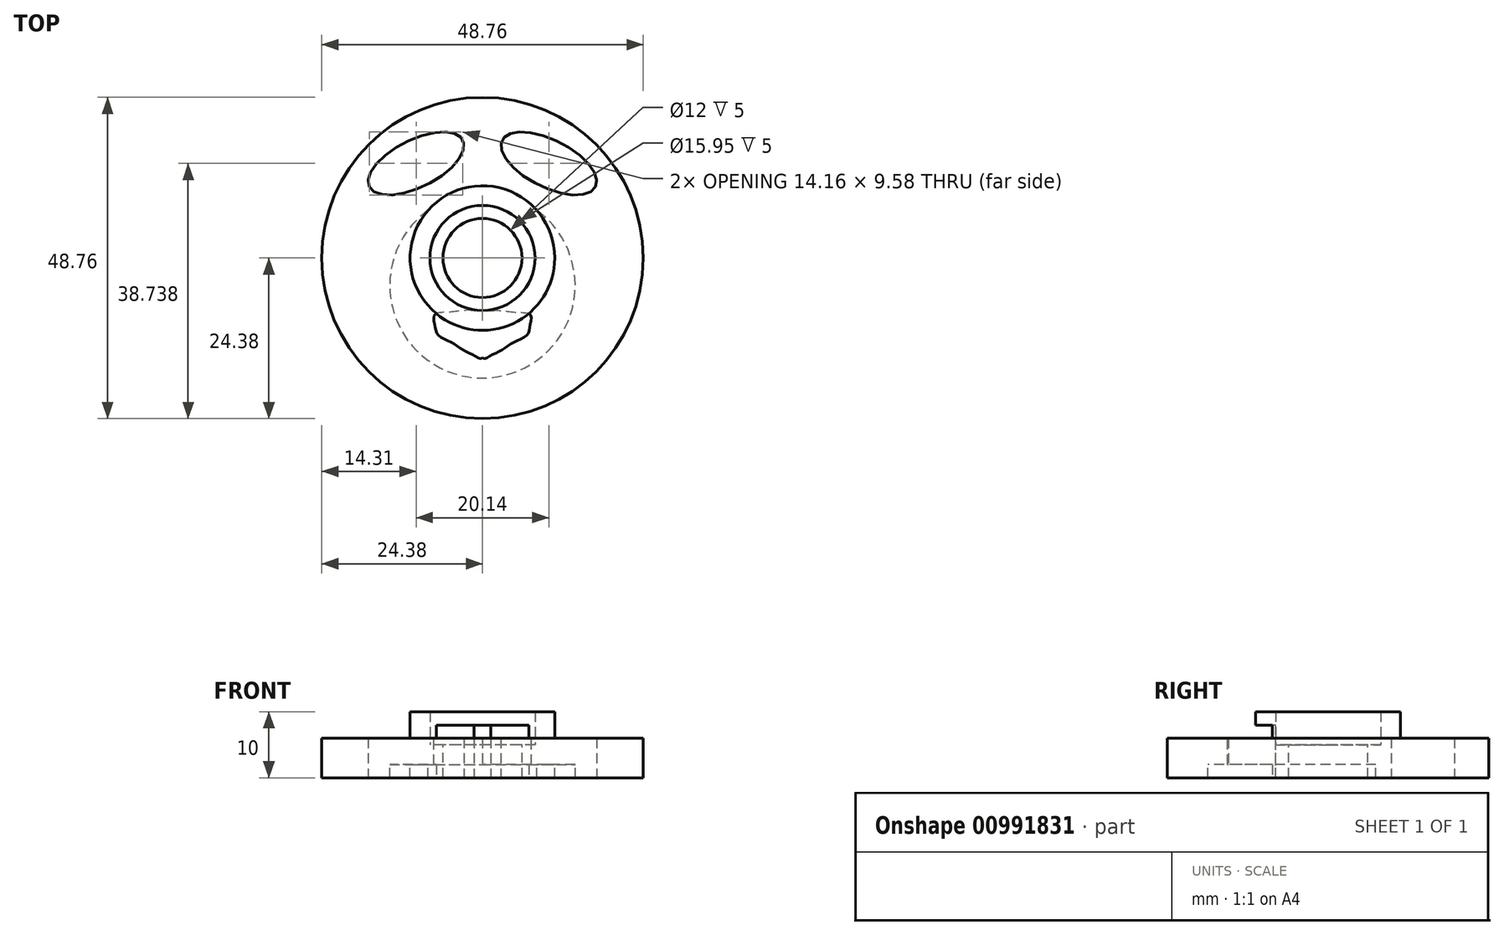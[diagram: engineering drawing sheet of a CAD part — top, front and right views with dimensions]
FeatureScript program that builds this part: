
annotation { "Feature Type Name" : "Feature", "Feature Type Description" : "" }
export const myFeature = defineFeature(function(context is Context, id is Id, definition is map)
    precondition{}
    {
        {
            var Q0;
            Q0=qCreatedBy(makeId("Top.planeOp"),FACE);
            var sketch = newSketch(context, id + "F0", { "sketchPlane" : qUnion([Q0])});
            skCircle(sketch, "E0", {"center": v(0, 0) * mm, "radius": 24.38 * mm});
            skSolve(sketch);
        }
        {
            var Q0;
            Q0=makeQuery(id+"F0.imprint","IMPRINT",FACE,{"disambiguationData":[TD([[makeQuery(id+"F0.imprint","IMPRINT",EDGE,{"derivedFrom":sQuery(id+"F0.wireOp",EDGE,"E0")}),1.0]])]});
            extrude(context, id + "F1", {"entities" : qUnion([Q0]), "depth" : 4 * mm, "offsetDistance" : 25.4 * mm});
        }
        {
            var Q0;
            Q0=makeQuery(id+"F1.opExtrude","CAP_FACE",FACE,{"disambiguationData":[OSD([sQuery(id+"F0.wireOp",EDGE,"E0"),sQuery(id+"F0.wireOp",EDGE,"n39IqKt5-bk1q-LU1x-fgod-8OyBNiFTd7FZ")])],"isStart":false});
            var sketch = newSketch(context, id + "F2", { "sketchPlane" : qUnion([Q0])});
            skCircle(sketch, "E1", {"center": v(0, 0) * mm, "radius": 7.97 * mm});
            skCircle(sketch, "E2.0", {"center": v(0, 0) * mm, "radius": 10.97 * mm});
            skSolve(sketch);
        }
        {
            var Q0;
            Q0=qSketchRegion(id+"F2",true);
            extrude(context, id + "F3", {"entities" : qUnion([Q0]), "operationType" : NewBodyOperationType.ADD, "depth" : 4 * mm, "offsetDistance" : 25.4 * mm});
        }
        {
            var Q0;
            Q0=makeQuery(id+"F3.boolean.opBoolean","SPLIT",FACE,{"disambiguationData":[TD([makeQuery(id+"F3.opExtrude","SWEPT_FACE",FACE,{"disambiguationData":[OSD([sQuery(id+"F2.wireOp",EDGE,"E1")])]})])],"derivedFrom":makeQuery(id+"F1.opExtrude","CAP_FACE",FACE,{"disambiguationData":[OSD([sQuery(id+"F0.wireOp",EDGE,"E0")])],"isStart":false})});
            var sketch = newSketch(context, id + "F4", { "sketchPlane" : qUnion([Q0])});
            skCircle(sketch, "E3", {"center": v(0, 0) * mm, "radius": 6 * mm});
            skSolve(sketch);
        }
        {
            var Q0;
            Q0=makeQuery(id+"F4.imprint","IMPRINT",FACE,{"disambiguationData":[TD([[makeQuery(id+"F4.imprint","IMPRINT",EDGE,{"derivedFrom":sQuery(id+"F4.wireOp",EDGE,"E3")}),1.0]])]});
            var Q1;
            Q1=makeQuery(id+"F4.imprint","IMPRINT",FACE,{"disambiguationData":[TD([[makeQuery(id+"F4.imprint","IMPRINT",EDGE,{"derivedFrom":makeQuery(id+"FgYK8jIepfClWtA_1.opExtrude","CAP_EDGE",EDGE,{"disambiguationData":[OSD([sQuery(id+"F8DXjnVyigKkjng_1.wireOp",EDGE,"EUjAMsCd-Zx2B-3j4q-cP5o-T3GrjTijNDqK")])],"isStart":false})}),1.0]])]});
            extrude(context, id + "F5", {"entities" : qUnion([Q0, Q1]), "operationType" : NewBodyOperationType.REMOVE, "oppositeDirection" : true, "depth" : 9 * mm, "offsetDistance" : 25.4 * mm});
        }
        {
            var Q0;
            Q0=qCreatedBy(makeId("Front.planeOp"),FACE);
            var sketch = newSketch(context, id + "F6", { "sketchPlane" : qUnion([Q0])});
            skCircle(sketch, "E4", {"center": v(-24.38, 2) * mm, "radius": 1.5 * mm});
            skLineSegment(sketch, "E5.bottom", {"start": v(-22.88, 0.65) * mm, "end": v(-25.02, 0.65) * mm});
            skLineSegment(sketch, "E5.top", {"start": v(-22.88, 3.35) * mm, "end": v(-25.02, 3.35) * mm});
            skLineSegment(sketch, "E5.left", {"start": v(-22.88, 0.65) * mm, "end": v(-22.88, 3.35) * mm});
            skLineSegment(sketch, "E5.right", {"start": v(-25.73, 1.35) * mm, "end": v(-25.73, 2.65) * mm});
            skLineSegment(sketch, "E6", {"start": v(0, 19.1) * mm, "end": v(0, -12.61) * mm, "construction": true});
            skLineSegment(sketch, "E7", {"start": v(-24.37, 3.35) * mm, "end": v(-22.88, 2) * mm});
            skLineSegment(sketch, "E8", {"start": v(-22.88, 2) * mm, "end": v(-24.38, 0.65) * mm});
            skLineSegment(sketch, "E9", {"start": v(-24.38, 0.65) * mm, "end": v(-24.37, 3.35) * mm});
            skSolve(sketch);
        }
        {
            var Q0;
            {var subQ0=sQuery(id+"F6.wireOp",EDGE,"E5.top");var subQ1=sQuery(id+"F6.wireOp",EDGE,"E4");var subQ2=makeQuery(id+"F6.imprint","INTERSECT",VERTEX,{"disambiguationData":[OD(0.0)],"derivedFrom":[subQ1,subQ0]});Q0=makeQuery(id+"F6.imprint","IMPRINT",FACE,{"disambiguationData":[TD([[makeQuery(id+"F6.imprint","IMPRINT",EDGE,{"disambiguationData":[TD([[subQ2,1.0]])],"derivedFrom":subQ1}),1.0]])]});}
            var Q1;
            {var subQ0=sQuery(id+"F6.wireOp",EDGE,"E5.bottom");var subQ1=sQuery(id+"F6.wireOp",EDGE,"E4");var subQ2=makeQuery(id+"F6.imprint","INTERSECT",VERTEX,{"disambiguationData":[OD(0.0)],"derivedFrom":[subQ1,subQ0]});Q1=makeQuery(id+"F6.imprint","IMPRINT",FACE,{"disambiguationData":[TD([[makeQuery(id+"F6.imprint","IMPRINT",EDGE,{"disambiguationData":[TD([[subQ2,-1.0]])],"derivedFrom":subQ1}),1.0]])]});}
            var Q2;
            {var subQ4=sQuery(id+"F6.wireOp",EDGE,"E5.right");Q2=makeQuery(id+"F6.imprint","IMPRINT",FACE,{"disambiguationData":[TD([[makeQuery(id+"F6.imprint","IMPRINT",EDGE,{"derivedFrom":subQ4}),-1.0]])]});}
            var Q3;
            {var subQ0=sQuery(id+"F6.wireOp",EDGE,"E7");Q3=makeQuery(id+"F6.imprint","IMPRINT",FACE,{"disambiguationData":[TD([[makeQuery(id+"F6.imprint","IMPRINT",EDGE,{"derivedFrom":subQ0}),1.0]])]});}
            var Q4;
            Q4=makeQuery(id+"F6.imprint","IMPRINT",FACE,{"disambiguationData":[TD([[makeQuery(id+"F6.imprint","IMPRINT",EDGE,{"derivedFrom":sQuery(id+"F6.wireOp",EDGE,"E7")}),-1.0]])]});
            var Q5;
            {var subQ0=sQuery(id+"F6.wireOp",EDGE,"E8");Q5=makeQuery(id+"F6.imprint","IMPRINT",FACE,{"disambiguationData":[TD([[makeQuery(id+"F6.imprint","IMPRINT",EDGE,{"derivedFrom":subQ0}),1.0]])]});}
            var Q6;
            Q6=sQuery(id+"F6.wireOp",EDGE,"E6");
            revolve(context, id + "F7", {"operationType" : NewBodyOperationType.REMOVE, "surfaceOperationType" : NewSurfaceOperationType.NEW, "entities" : qUnion([Q0, Q1, Q2, Q3, Q4, Q5]), "axis" : qUnion([Q6]), "revolveType" : RevolveType.FULL, "oppositeDirection" : true});
        }
        {
            var Q0;
            Q0=makeQuery(id+"F3.boolean.opBoolean","SPLIT",FACE,{"disambiguationData":[TD([makeQuery(id+"F3.opExtrude","SWEPT_FACE",FACE,{"disambiguationData":[OSD([sQuery(id+"F2.wireOp",EDGE,"E1")])]})])],"derivedFrom":makeQuery(id+"F1.opExtrude","CAP_FACE",FACE,{"disambiguationData":[OSD([sQuery(id+"F0.wireOp",EDGE,"E0")])],"isStart":false})});
            extrude(context, id + "F8", {"entities" : qUnion([Q0]), "operationType" : NewBodyOperationType.REMOVE, "oppositeDirection" : true, "depth" : 1 * mm, "offsetDistance" : 25 * mm});
        }
        {
            var Q0;
            {var subQ0=sQuery(id+"F0.wireOp",EDGE,"E0");Q0=makeQuery(id+"F3.boolean.opBoolean","SPLIT",FACE,{"disambiguationData":[TD([makeQuery(id+"F1.opExtrude","SWEPT_FACE",FACE,{"disambiguationData":[OSD([subQ0])]})])],"derivedFrom":makeQuery(id+"F1.opExtrude","CAP_FACE",FACE,{"disambiguationData":[OSD([subQ0])],"isStart":false})});}
            var sketch = newSketch(context, id + "F9", { "sketchPlane" : qUnion([Q0])});
            skEllipse(sketch, "E10", {"center": v(-10.07, 14.36) * mm, "majorRadius": 7.91 * mm, "minorRadius": 3.61 * mm, "majorAxis": v(-0.9, -0.45)});
            skEllipse(sketch, "E11.MirrorC", {"center": v(10.07, 14.36) * mm, "majorRadius": 7.91 * mm, "minorRadius": 3.61 * mm, "majorAxis": v(0.9, -0.45)});
            skCircle(sketch, "E12", {"center": v(0, 4.7) * mm, "radius": 19.13 * mm});
            skCircle(sketch, "E13", {"center": v(0, -4.15) * mm, "radius": 14.06 * mm});
            skSolve(sketch);
        }
        {
            var Q0;
            Q0=makeQuery(id+"F9.imprint","IMPRINT",FACE,{"disambiguationData":[TD([[makeQuery(id+"F9.imprint","IMPRINT",EDGE,{"derivedFrom":sQuery(id+"F9.wireOp",EDGE,"E10")}),1.0]])]});
            var Q1;
            Q1=makeQuery(id+"F9.imprint","IMPRINT",FACE,{"disambiguationData":[TD([[makeQuery(id+"F9.imprint","IMPRINT",EDGE,{"derivedFrom":sQuery(id+"F9.wireOp",EDGE,"E11.MirrorC")}),1.0]])]});
            extrude(context, id + "F10", {"entities" : qUnion([Q0, Q1]), "operationType" : NewBodyOperationType.REMOVE, "oppositeDirection" : true, "depth" : 25 * mm, "offsetDistance" : 25 * mm});
        }
        {
            var Q0;
            Q0=makeQuery(id+"F9.imprint","IMPRINT",FACE,{"disambiguationData":[TD([[makeQuery(id+"F9.imprint","IMPRINT",EDGE,{"derivedFrom":sQuery(id+"F9.wireOp",EDGE,"E10")}),-1.0]])]});
            extrude(context, id + "F11", {"entities" : qUnion([Q0]), "operationType" : NewBodyOperationType.ADD, "oppositeDirection" : true, "depth" : 6 * mm, "offsetDistance" : 25 * mm});
        }
        {
            var Q0;
            {var subQ0=sQuery(id+"F9.wireOp",EDGE,"E13");var subQ1=sQuery(id+"F9.wireOp",EDGE,"E12");var subQ2=makeQuery(id+"F9.imprint","INTERSECT",VERTEX,{"disambiguationData":[OD(0.0)],"derivedFrom":[subQ1,subQ0]});Q0=makeQuery(id+"F9.imprint","IMPRINT",FACE,{"disambiguationData":[TD([[makeQuery(id+"F9.imprint","IMPRINT",EDGE,{"disambiguationData":[TD([[subQ2,-1.0]])],"derivedFrom":subQ1}),1.0]])]});}
            var Q1;
            {var subQ0=sQuery(id+"F9.wireOp",EDGE,"E13");var subQ1=sQuery(id+"F9.wireOp",EDGE,"E12");var subQ2=makeQuery(id+"F9.imprint","INTERSECT",VERTEX,{"disambiguationData":[OD(0.0)],"derivedFrom":[subQ1,subQ0]});Q1=makeQuery(id+"F9.imprint","IMPRINT",FACE,{"disambiguationData":[TD([[makeQuery(id+"F9.imprint","IMPRINT",EDGE,{"disambiguationData":[TD([[subQ2,-1.0]])],"derivedFrom":subQ1}),-1.0]])]});}
            extrude(context, id + "F12", {"entities" : qUnion([Q0, Q1]), "operationType" : NewBodyOperationType.ADD, "oppositeDirection" : true, "depth" : 6 * mm, "offsetDistance" : 25 * mm});
        }
        {
            var Q0;
            Q0=makeQuery(id+"F12.boolean.opBoolean","SPLIT",FACE,{"disambiguationData":[TD([makeQuery(id+"F5.boolean.opBoolean","COPY",FACE,{"derivedFrom":makeQuery(id+"F5.opExtrude","SWEPT_FACE",FACE,{"disambiguationData":[OSD([sQuery(id+"F4.wireOp",EDGE,"E3")])]})})])],"derivedFrom":makeQuery(id+"F1.opExtrude","CAP_FACE",FACE,{"disambiguationData":[OSD([sQuery(id+"F0.wireOp",EDGE,"E0")])],"isStart":true})});
            var sketch = newSketch(context, id + "F13", { "sketchPlane" : qUnion([Q0])});
            skCircle(sketch, "E14", {"center": v(0, 0) * mm, "radius": 6 * mm});
            skCircle(sketch, "E15", {"center": v(0, 0) * mm, "radius": 10.97 * mm});
            skSolve(sketch);
        }
        {
            var Q0;
            Q0 = qSketchRegion(id + "F13", true);
            extrude(context, id + "F14", {"entities" : qUnion([Q0]), "operationType" : NewBodyOperationType.ADD, "depth" : 2 * mm, "offsetDistance" : 25 * mm});
        }
        {
            var Q0;
            {var subQ0=sQuery(id+"F9.wireOp",EDGE,"E13");var subQ1=sQuery(id+"F2.wireOp",EDGE,"E2.0");Q0=makeQuery(id+"F14.boolean.opBoolean","MERGE",FACE,{"derivedFrom":[makeQuery(id+"F12.boolean.opBoolean","MERGE",FACE,{"derivedFrom":[makeQuery(id+"F11.opExtrude","CAP_FACE",FACE,{"disambiguationData":[OSD([subQ1,sQuery(id+"F9.wireOp",EDGE,"E10"),sQuery(id+"F9.wireOp",EDGE,"E11.MirrorC"),sQuery(id+"F9.wireOp",EDGE,"E12"),subQ0])],"isStart":false}),makeQuery(id+"F12.opExtrude","CAP_FACE",FACE,{"disambiguationData":[OSD([subQ1,subQ0])],"isStart":false})]}),makeQuery(id+"F14.opExtrude","CAP_FACE",FACE,{"disambiguationData":[OSD([sQuery(id+"F13.wireOp",EDGE,"E14"),sQuery(id+"F13.wireOp",EDGE,"E15")])],"isStart":false})]});}
            var sketch = newSketch(context, id + "F15", { "sketchPlane" : qUnion([Q0])});
            skFitSpline(sketch, "E16", {"points": [v(0, 8.8) * mm, v(4.59, 8.18) * mm, v(7.28, 8.64) * mm, v(7.22, 10.24) * mm, v(6.76, 11.67) * mm, v(4.7, 12.81) * mm, v(2.87, 14.02) * mm, v(0.98, 14.93) * mm, v(0, 15.16) * mm, v(0, 8.8) * mm]});
            skFitSpline(sketch, "E17.MirrorC", {"points": [v(0, 8.8) * mm, v(-4.59, 8.18) * mm, v(-7.28, 8.64) * mm, v(-7.22, 10.24) * mm, v(-6.76, 11.67) * mm, v(-4.7, 12.81) * mm, v(-2.87, 14.02) * mm, v(-0.98, 14.93) * mm, v(0, 15.16) * mm, v(0, 8.8) * mm]});
            skLineSegment(sketch, "E18", {"start": v(1.27, 8.01) * mm, "end": v(-1.27, 8.01) * mm});
            skSolve(sketch);
        }
        {
            var Q0;
            Q0 = qSketchRegion(id + "F15", true);
            extrude(context, id + "F16", {"entities" : qUnion([Q0]), "operationType" : NewBodyOperationType.REMOVE, "oppositeDirection" : true, "depth" : 8 * mm, "offsetDistance" : 25 * mm});
        }
    });
